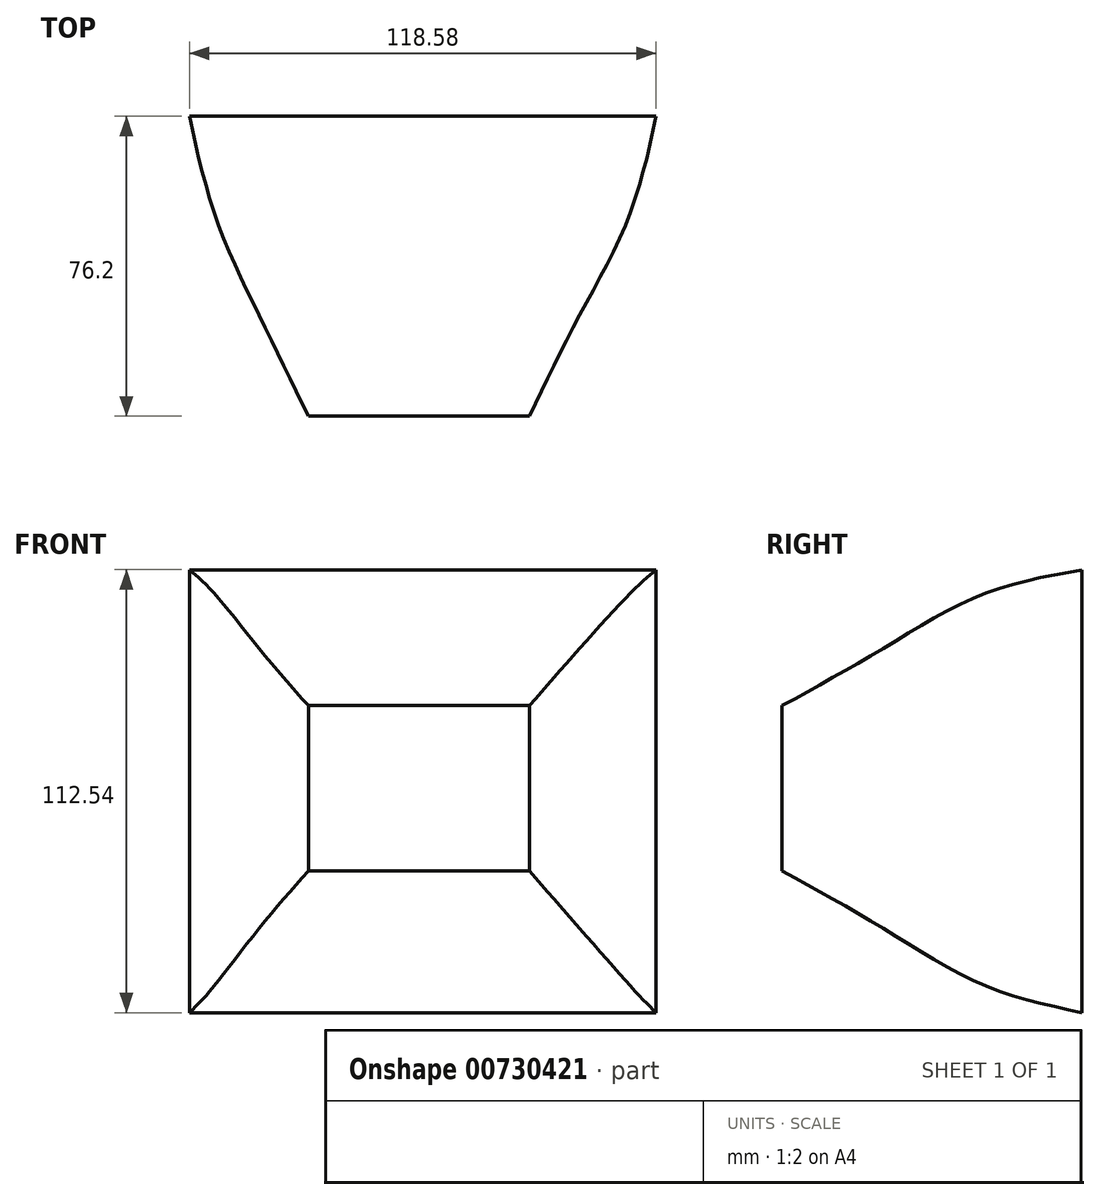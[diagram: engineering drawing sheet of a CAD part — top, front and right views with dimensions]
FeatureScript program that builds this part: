
annotation { "Feature Type Name" : "Feature", "Feature Type Description" : "" }
export const myFeature = defineFeature(function(context is Context, id is Id, definition is map)
    precondition{}
    {
        {
            var Q0;
            Q0=qCreatedBy(makeId("Front.planeOp"),FACE);
            cPlane(context, id + "F0", {"entities" : qUnion([Q0]), "cplaneType" : CPlaneType.OFFSET, "offset" : 25.4 * mm, "width" : 152.4 * mm, "height" : 152.4 * mm});
        }
        {
            var Q0;
            Q0=qCreatedBy(id+"F0.planeOp",FACE);
            var sketch = newSketch(context, id + "F1", { "sketchPlane" : qUnion([Q0])});
            skLineSegment(sketch, "E0.bottom", {"start": v(-60, 56.27) * mm, "end": v(58.57, 56.27) * mm});
            skLineSegment(sketch, "E0.top", {"start": v(-60, -56.27) * mm, "end": v(58.57, -56.27) * mm});
            skLineSegment(sketch, "E0.left", {"start": v(-60, 56.27) * mm, "end": v(-60, -56.27) * mm});
            skLineSegment(sketch, "E0.right", {"start": v(58.57, 56.27) * mm, "end": v(58.57, -56.27) * mm});
            skSolve(sketch);
        }
        {
            var Q0;
            Q0=qCreatedBy(id+"F0.planeOp",FACE);
            cPlane(context, id + "F2", {"entities" : qUnion([Q0]), "cplaneType" : CPlaneType.OFFSET, "offset" : 25.4 * mm, "width" : 152.4 * mm, "height" : 152.4 * mm});
        }
        {
            var Q0;
            Q0=qCreatedBy(id+"F2.planeOp",FACE);
            var sketch = newSketch(context, id + "F3", { "sketchPlane" : qUnion([Q0])});
            skLineSegment(sketch, "E1.bottom", {"start": v(-53.39, 49.93) * mm, "end": v(51.66, 49.93) * mm});
            skLineSegment(sketch, "E1.top", {"start": v(-53.39, -49.07) * mm, "end": v(51.66, -49.07) * mm});
            skLineSegment(sketch, "E1.left", {"start": v(-53.39, 49.93) * mm, "end": v(-53.39, -49.07) * mm});
            skLineSegment(sketch, "E1.right", {"start": v(51.66, 49.93) * mm, "end": v(51.66, -49.07) * mm});
            skSolve(sketch);
        }
        {
            var Q0;
            Q0=qCreatedBy(id+"F2.planeOp",FACE);
            cPlane(context, id + "F4", {"entities" : qUnion([Q0]), "cplaneType" : CPlaneType.OFFSET, "offset" : 25.4 * mm, "width" : 152.4 * mm, "height" : 152.4 * mm});
        }
        {
            var Q0;
            Q0=qCreatedBy(id+"F4.planeOp",FACE);
            var sketch = newSketch(context, id + "F5", { "sketchPlane" : qUnion([Q0])});
            skLineSegment(sketch, "E2.bottom", {"start": v(-42.16, 36.12) * mm, "end": v(39, 36.12) * mm});
            skLineSegment(sketch, "E2.top", {"start": v(-42.16, -34.68) * mm, "end": v(39, -34.68) * mm});
            skLineSegment(sketch, "E2.left", {"start": v(-42.16, 36.12) * mm, "end": v(-42.16, -34.68) * mm});
            skLineSegment(sketch, "E2.right", {"start": v(39, 36.12) * mm, "end": v(39, -34.68) * mm});
            skSolve(sketch);
        }
        {
            var Q0;
            Q0=qCreatedBy(id+"F4.planeOp",FACE);
            cPlane(context, id + "F6", {"entities" : qUnion([Q0]), "cplaneType" : CPlaneType.OFFSET, "offset" : 25.4 * mm, "width" : 152.4 * mm, "height" : 152.4 * mm});
        }
        {
            var Q0;
            Q0=qCreatedBy(id+"F6.planeOp",FACE);
            var sketch = newSketch(context, id + "F7", { "sketchPlane" : qUnion([Q0])});
            skLineSegment(sketch, "E3.bottom", {"start": v(-29.79, 21.73) * mm, "end": v(26.33, 21.73) * mm});
            skLineSegment(sketch, "E3.top", {"start": v(-29.79, -20.3) * mm, "end": v(26.33, -20.3) * mm});
            skLineSegment(sketch, "E3.left", {"start": v(-29.79, 21.73) * mm, "end": v(-29.79, -20.3) * mm});
            skLineSegment(sketch, "E3.right", {"start": v(26.33, 21.73) * mm, "end": v(26.33, -20.3) * mm});
            skSolve(sketch);
        }
        {
            var Q0;
            Q0 = qSketchRegion(id + "F1", true);
            var Q1;
            Q1 = qSketchRegion(id + "F3", true);
            var Q2;
            Q2 = qSketchRegion(id + "F5", true);
            var Q3;
            Q3 = qSketchRegion(id + "F7", true);
            loft(context, id + "F8", {"sheetProfilesArray" : [{ "sheetProfileEntities" : qUnion([Q0]) }, { "sheetProfileEntities" : qUnion([Q1]) }, { "sheetProfileEntities" : qUnion([Q2]) }, { "sheetProfileEntities" : qUnion([Q3]) }]});
        }
    });
